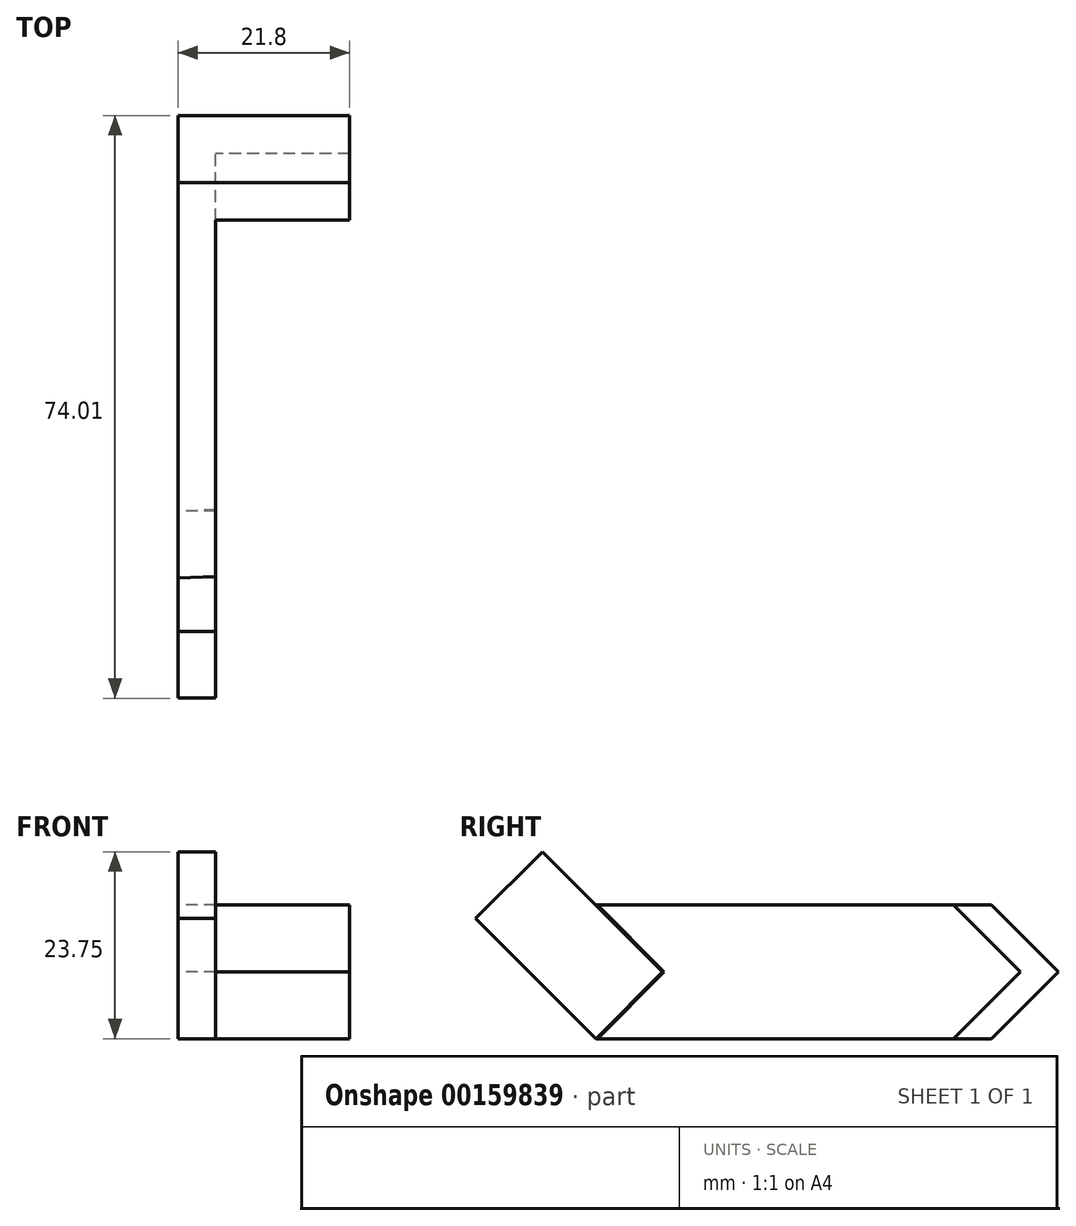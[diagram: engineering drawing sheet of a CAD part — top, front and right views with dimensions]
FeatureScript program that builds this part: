
annotation { "Feature Type Name" : "Feature", "Feature Type Description" : "" }
export const myFeature = defineFeature(function(context is Context, id is Id, definition is map)
    precondition{}
    {
        {
            var Q0;
            Q0=qCreatedBy(makeId("Top.planeOp"),FACE);
            var sketch = newSketch(context, id + "F0", { "sketchPlane" : qUnion([Q0])});
            skLineSegment(sketch, "E0", {"start": v(0, 24.78) * mm, "end": v(-17, 24.78) * mm});
            skLineSegment(sketch, "E1", {"start": v(-17, 24.78) * mm, "end": v(-17, -20.48) * mm});
            skLineSegment(sketch, "E2.0", {"start": v(-21.8, 29.58) * mm, "end": v(-21.8, -20.68) * mm});
            skLineSegment(sketch, "E2.1", {"start": v(0, 29.58) * mm, "end": v(-21.8, 29.58) * mm});
            skLineSegment(sketch, "E3", {"start": v(0, 29.58) * mm, "end": v(0, 24.78) * mm});
            skLineSegment(sketch, "E4", {"start": v(-17, -20.48) * mm, "end": v(-21.8, -20.68) * mm});
            skSolve(sketch);
        }
        {
            var Q0;
            Q0=qCreatedBy(makeId("Right.planeOp"),FACE);
            var sketch = newSketch(context, id + "F1", { "sketchPlane" : qUnion([Q0])});
            skLineSegment(sketch, "E5", {"start": v(0, 0) * mm, "end": v(8.49, 8.49) * mm});
            skSolve(sketch);
        }
        {
            var Q0;
            Q0 = qSketchRegion(id + "F0", true);
            var Q1;
            Q1 = qConstructionFilter(qBodyType(qCreatedBy(id + "F1" ,EDGE), BodyType.WIRE), ConstructionObject.NO);
            sweep(context, id + "F2", {"profiles" : qUnion([Q0]), "path" : qUnion([Q1])});
        }
        {
            var Q0;
            Q0=makeQuery(id+"F2.opSweep","CAP_FACE",FACE,{"disambiguationData":[OSD([sQuery(id+"F0.wireOp",EDGE,"E0"),sQuery(id+"F0.wireOp",EDGE,"E1"),sQuery(id+"F0.wireOp",EDGE,"E2.0"),sQuery(id+"F0.wireOp",EDGE,"E2.1"),sQuery(id+"F0.wireOp",EDGE,"E3"),sQuery(id+"F0.wireOp",EDGE,"E4"),sQuery(id+"F1.wireOp",VERTEX,"E5.end")])],"isStart":false});
            var sketch = newSketch(context, id + "F3", { "sketchPlane" : qUnion([Q0])});
            skLineSegment(sketch, "E6.0.0", {"start": v(-17, 33.26) * mm, "end": v(0, 33.26) * mm});
            skLineSegment(sketch, "E6.0.1", {"start": v(0, 33.26) * mm, "end": v(0, 38.06) * mm});
            skLineSegment(sketch, "E6.0.2", {"start": v(0, 38.06) * mm, "end": v(-21.8, 38.06) * mm});
            skLineSegment(sketch, "E6.0.3", {"start": v(-21.8, 38.06) * mm, "end": v(-21.8, -12.2) * mm});
            skLineSegment(sketch, "E6.0.4", {"start": v(-21.8, -12.2) * mm, "end": v(-17, -12) * mm});
            skLineSegment(sketch, "E6.0.5", {"start": v(-17, -12) * mm, "end": v(-17, 33.26) * mm});
            skSolve(sketch);
        }
        {
            var Q0;
            Q0=qCreatedBy(makeId("Right.planeOp"),FACE);
            var sketch = newSketch(context, id + "F4", { "sketchPlane" : qUnion([Q0])});
            skPoint(sketch, "E7.0", {"position": v(8.49, 8.49) * mm});
            skLineSegment(sketch, "E8", {"start": v(8.49, 8.49) * mm, "end": v(0, 16.97) * mm});
            skSolve(sketch);
        }
        {
            var Q0;
            Q0 = qSketchRegion(id + "F3", true);
            var Q1;
            Q1 = qConstructionFilter(qBodyType(qCreatedBy(id + "F4" ,EDGE), BodyType.WIRE), ConstructionObject.NO);
            sweep(context, id + "F5", {"operationType" : NewBodyOperationType.ADD, "profiles" : qUnion([Q0]), "path" : qUnion([Q1])});
        }
        {
            var Q0;
            Q0=makeQuery(id+"F5.boolean.opBoolean","MERGE",FACE,{"derivedFrom":[makeQuery(id+"F2.opSweep","SWEPT_FACE",FACE,{"disambiguationData":[OSD([sQuery(id+"F0.wireOp",EDGE,"E2.0"),sQuery(id+"F1.wireOp",EDGE,"E5")])]}),makeQuery(id+"F5.opSweep","SWEPT_FACE",FACE,{"disambiguationData":[OSD([sQuery(id+"F3.wireOp",EDGE,"E6.0.3"),sQuery(id+"F4.wireOp",EDGE,"E8")])]})]});
            var sketch = newSketch(context, id + "F6", { "sketchPlane" : qUnion([Q0])});
            skLineSegment(sketch, "E9", {"start": v(20.68, 16.97) * mm, "end": v(20.68, 0) * mm});
            skLineSegment(sketch, "E10", {"start": v(20.68, 0) * mm, "end": v(12.2, 8.49) * mm});
            skLineSegment(sketch, "E11", {"start": v(12.2, 8.49) * mm, "end": v(20.68, 16.97) * mm});
            skSolve(sketch);
        }
        {
            var Q0;
            Q0 = qSketchRegion(id + "F6", true);
            extrude(context, id + "F7", {"entities" : qUnion([Q0]), "oppositeDirection" : true, "depth" : 4.8 * mm});
        }
        {
            var Q0;
            Q0=makeQuery(id+"F7.opExtrude","CAP_FACE",FACE,{"disambiguationData":[OSD([sQuery(id+"F6.wireOp",EDGE,"E9"),sQuery(id+"F6.wireOp",EDGE,"E10"),sQuery(id+"F6.wireOp",EDGE,"E11")])],"isStart":false});
            var sketch = newSketch(context, id + "F8", { "sketchPlane" : qUnion([Q0])});
            skLineSegment(sketch, "E12", {"start": v(-20.68, 0) * mm, "end": v(-35.95, 15.27) * mm});
            skLineSegment(sketch, "E13", {"start": v(-20.68, 0) * mm, "end": v(-20.68, 16.97) * mm});
            skLineSegment(sketch, "E14", {"start": v(-20.68, 16.97) * mm, "end": v(-27.46, 23.75) * mm});
            skLineSegment(sketch, "E15", {"start": v(-35.95, 15.27) * mm, "end": v(-27.46, 23.75) * mm});
            skSolve(sketch);
        }
        {
            var Q0;
            Q0=makeQuery(id+"F8.imprint","IMPRINT",FACE,{"disambiguationData":[TD([[makeQuery(id+"F8.imprint","IMPRINT",EDGE,{"derivedFrom":sQuery(id+"F8.wireOp",EDGE,"E12")}),-1.0]])]});
            extrude(context, id + "F9", {"entities" : qUnion([Q0]), "operationType" : NewBodyOperationType.ADD, "oppositeDirection" : true, "depth" : 4.8 * mm});
        }
    });
